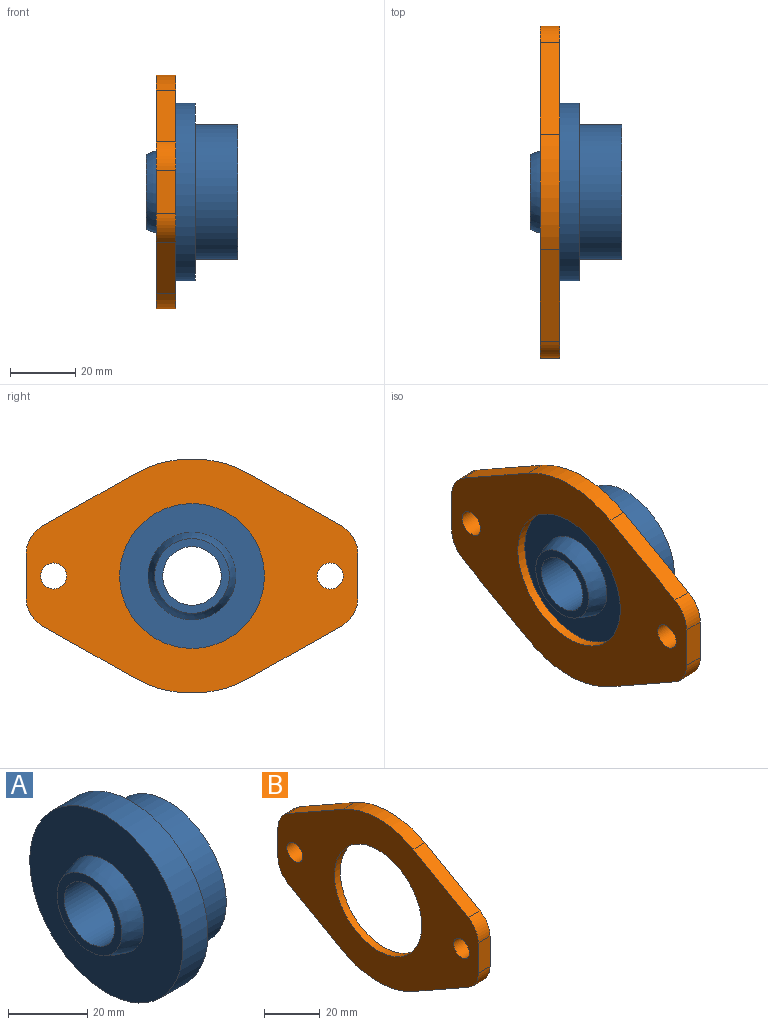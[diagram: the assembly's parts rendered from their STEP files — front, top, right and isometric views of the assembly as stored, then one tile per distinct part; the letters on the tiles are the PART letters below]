
ASSEMBLY  parts=2 mates=1
PART A: 10 faces, bbox 28x54.5x54.5 mm
  f0: plane 54.5x54.5mm, normal (-1,0,0), area 1764.6mm2, adj f1,f9
  f1: revolved ~26.9x26.9mm, area 500.1mm2, adj f0,f2
  f2: plane 23x23mm, normal (-1,0,0), area 161mm2, adj f1,f3
  f3: cylinder r=9mm len=23mm, axis (-1,0,0), area 1300.6mm2, adj f2,f4
  f4: plane 28x28mm, normal (1,0,0), area 361.3mm2, adj f3,f5
  f5: cylinder r=14mm len=28mm, axis (-1,0,0), area 439.8mm2, adj f4,f6
  f6: plane 41.5x41.5mm, normal (1,0,0), area 736.9mm2, adj f5,f7
  f7: cylinder r=20.75mm len=41.5mm, axis (-1,0,0), area 1694.9mm2, adj f6,f8
  f8: plane 54.5x54.5mm, normal (1,0,0), area 980.2mm2, adj f7,f9
  f9: cylinder r=27.25mm len=54.5mm, axis (-1,0,0), area 1541mm2, adj f0,f8
PART B: 19 faces, bbox 6x102x72 mm
  f0: cylinder r=27.25mm len=54.5mm, axis (-1,0,0), area 513.7mm2, adj f11,f14
  f1: plane 28.19x15.96mm, normal (0,-0.49,-0.87), area 194.4mm2, adj f10,f11,f12,f18
  f2: plane 13.34x6mm, normal (0,-1,0), area 80mm2, adj f11,f12,f15,f18
  f3: plane 28.19x15.96mm, normal (0,-0.49,0.87), area 194.4mm2, adj f4,f11,f12,f15
  f4: cylinder r=36mm len=35.47mm, axis (-1,0,0), area 222.5mm2, adj f3,f5,f11,f12
  f5: plane 28.19x15.96mm, normal (0,0.49,0.87), area 194.4mm2, adj f4,f11,f12,f16
  f6: plane 13.34x6mm, normal (0,1,0), area 80mm2, adj f11,f12,f16,f17
  f7: plane 28.19x15.96mm, normal (0,0.49,-0.87), area 194.4mm2, adj f10,f11,f12,f17
  f8: cylinder r=4mm len=8mm, axis (-1,0,0), area 150.8mm2, adj f11,f12
  f9: cylinder r=4mm len=8mm, axis (-1,0,0), area 150.8mm2, adj f11,f12
  f10: cylinder r=36mm len=35.47mm, axis (-1,0,0), area 222.5mm2, adj f1,f7,f11,f12
  f11: plane 102x72mm, normal (1,0,0), area 2906.9mm2, adj f0,f1,f2,f3,f4,f5,f6,f7
  f12: plane 102x72mm, normal (-1,0,0), area 3684.4mm2, adj f1,f2,f3,f4,f5,f6,f7,f8
  f13: cylinder r=22.25mm len=44.5mm, axis (-1,0,0), area 419.4mm2, adj f12,f14
  f14: plane 54.5x54.5mm, normal (1,0,0), area 777.5mm2, adj f0,f13
  f15: cylinder r=10mm len=8.7mm, axis (-1,0,0), area 63.3mm2, adj f2,f3,f11,f12
  f16: cylinder r=10mm len=8.7mm, axis (1,0,0), area 63.3mm2, adj f5,f6,f11,f12
  f17: cylinder r=10mm len=8.7mm, axis (-1,0,0), area 63.3mm2, adj f6,f7,f11,f12
  f18: cylinder r=10mm len=8.7mm, axis (1,0,0), area 63.3mm2, adj f1,f2,f11,f12
PLACE A t=(-42.84,-16.98,4.7)mm
PLACE B t=(-45.84,-16.98,4.7)mm
MATE fastened B.f0 <-> A.f3  axis (1,0,0) through (-42.84,-16.98,4.7)mm
